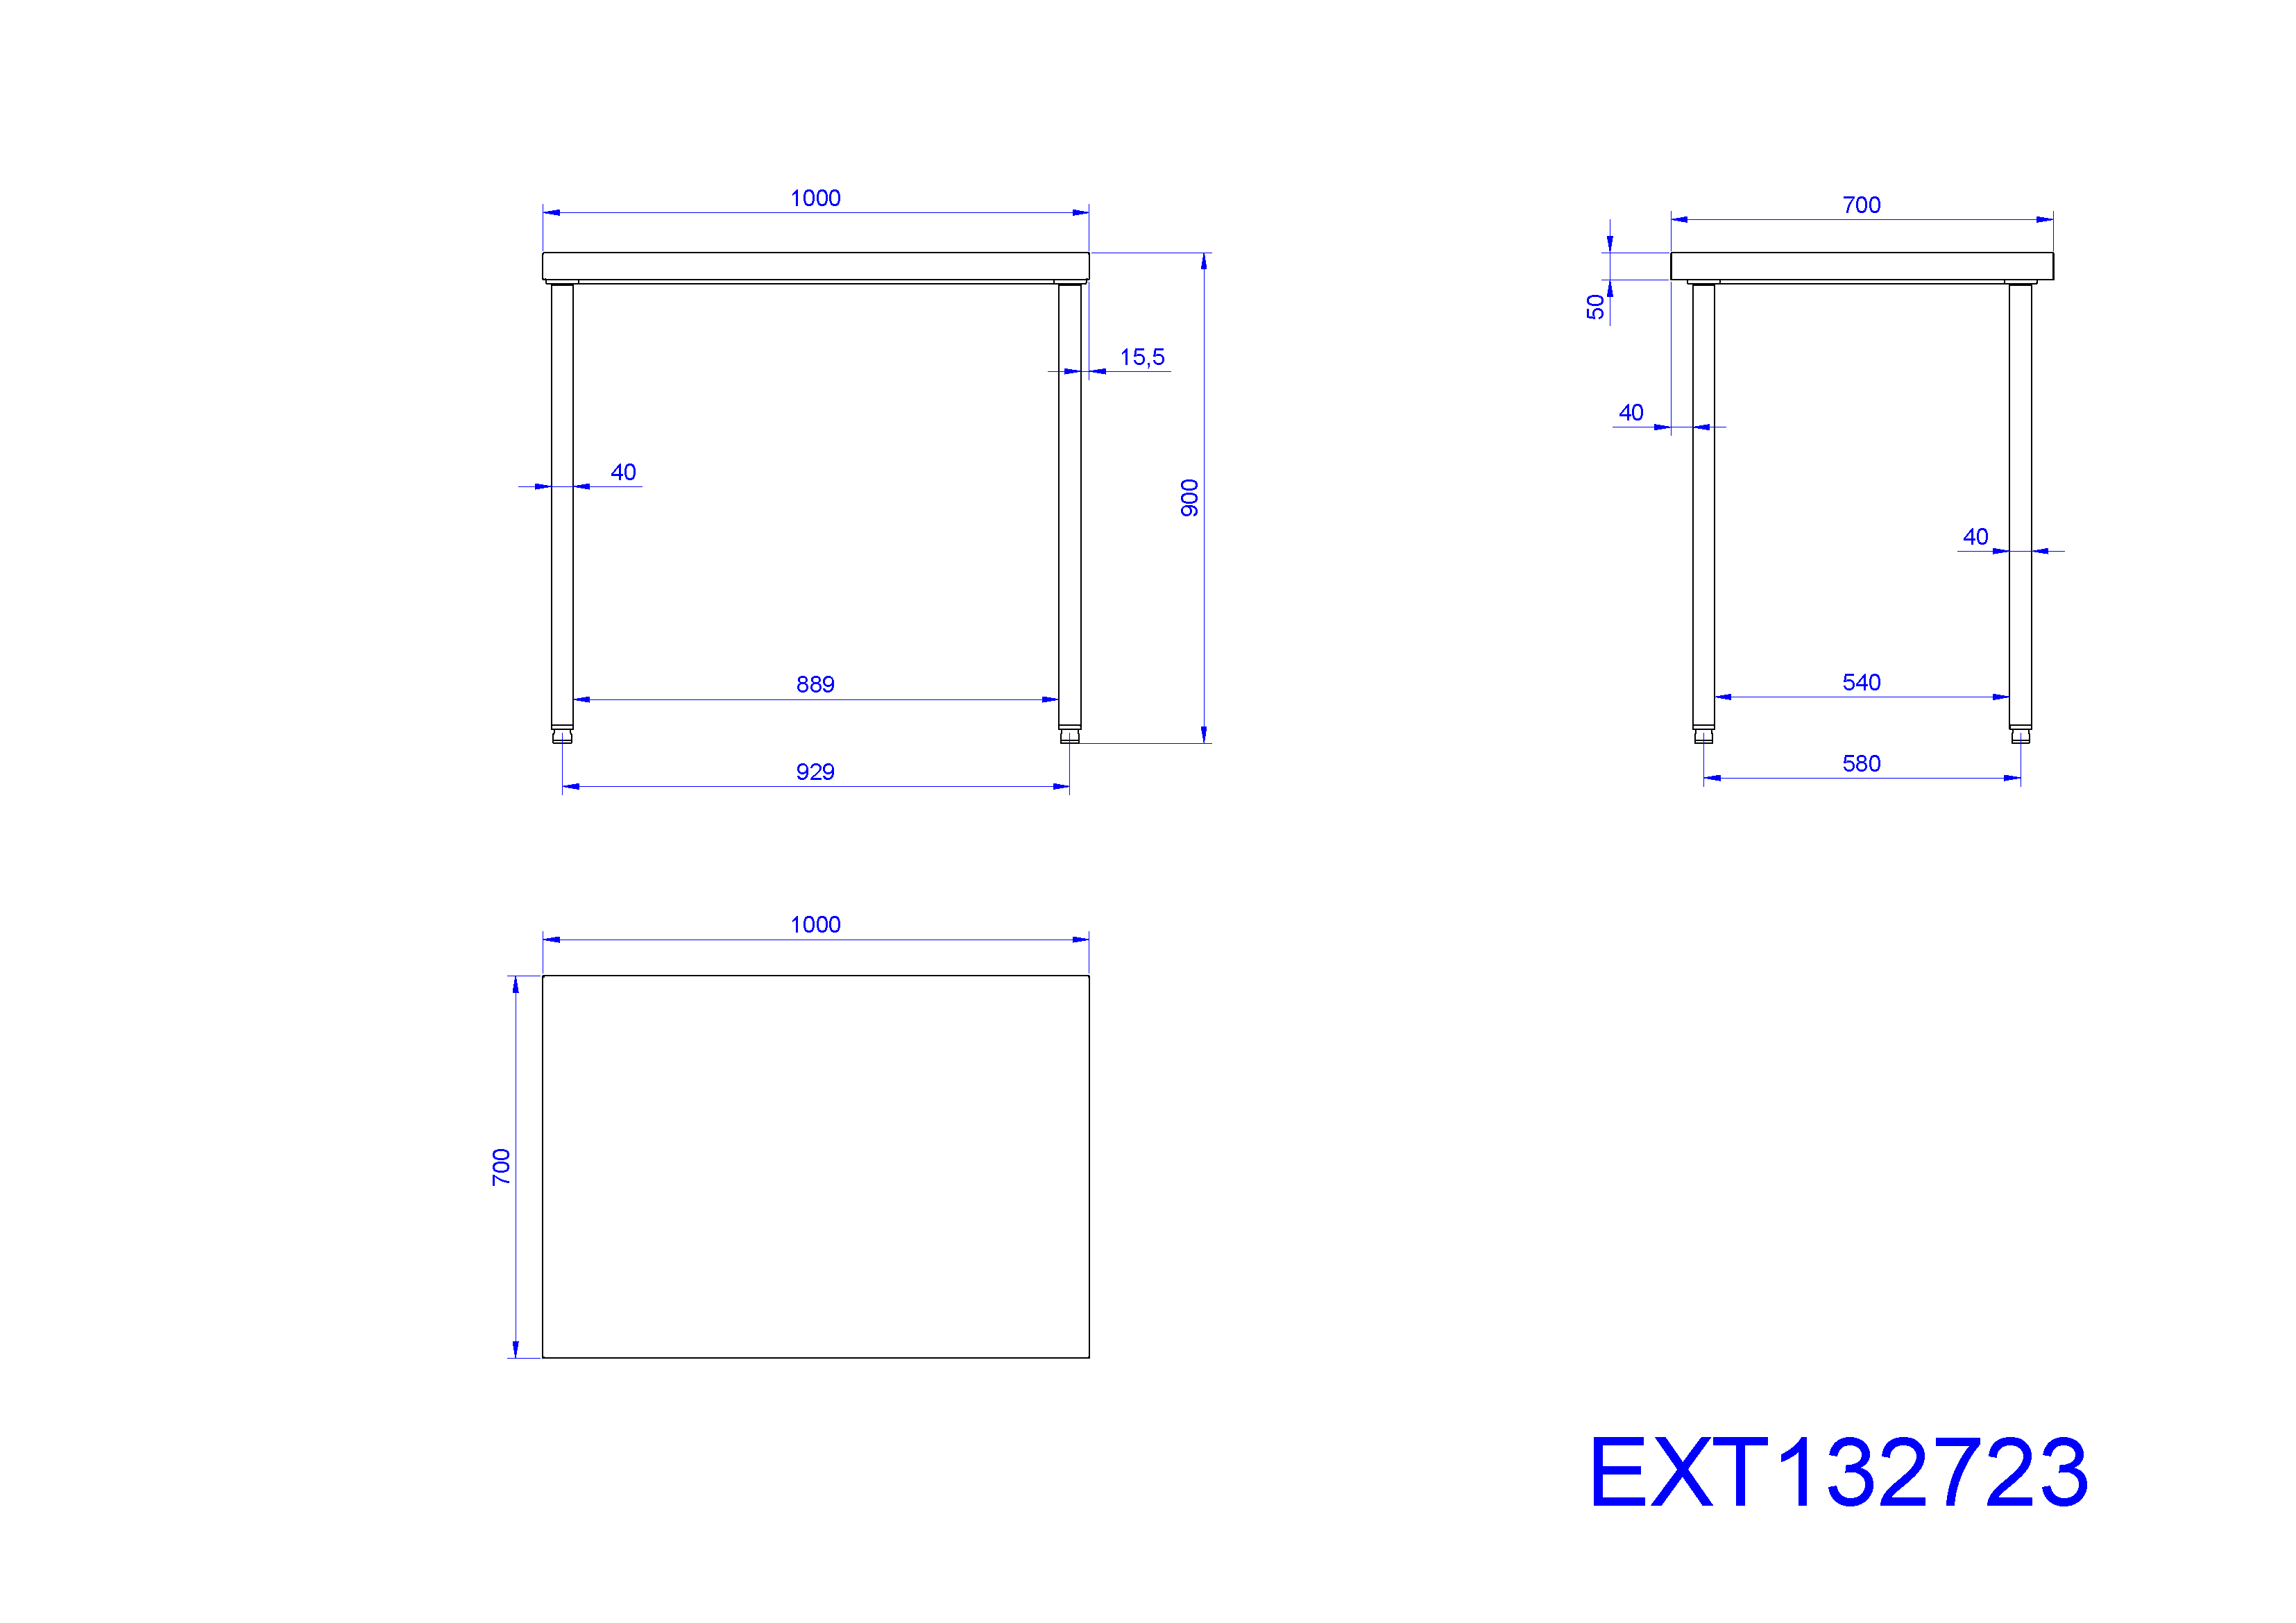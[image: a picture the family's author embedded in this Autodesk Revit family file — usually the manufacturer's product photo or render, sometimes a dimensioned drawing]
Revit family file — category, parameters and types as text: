
# Revit family: QF_ELECTROLUXPROFESSIONAL_132918_ML2S1217N
name_source: partatom
category: Attrezzature speciali
units: mm (PartAtom-declared; Revit-internal decimal feet)

## family parameters
Basato su piano di lavoro = No
Condiviso = No
Punto di calcolo locali = No
Quota connettore circolare = Usa diametro
Sempre verticale = Sì
Taglio con vuoti quando caricato = No
Tipo di parte = Normale

## types (1)
- Standard
    Accessory = Sì
    Cold Water Size = 0 mm
    Compressed Air Pressure = 0.0 Pa
    Compressed Air Size = 0 mm
    Compressed Air Volume = 0.0 L/s
    Condensate Return Size = 0 mm
    Cycle = 0 Hz
    Depth Actual = 700 mm  [stored 2.29659 ft]
    Descrizione = CUPBOARD SINK 2 BOWLS (500X500) 1200MM
    Direct Waste Size = 140 mm
    Gas Input Pressure = 0
    Gas KW = 0
    Gas Size = 0 mm
    HP = 0 HP
    Height Actual = 1000 mm  [stored 3.28084 ft]
    Hot Water Size = 0 mm
    Item Number = 132918
    Length Actual = 1200 mm
    Modello = ML2S1217N
    Phase = 0
    Produttore = Electrolux Professional
    Prospetto di default = 0 mm  [stored 0 ft]
    Refrigerant Compressor Remote = Sì
    Refrigeration Liquid Line Size = 0 mm  [stored 0 ft]
    Refrigeration Suction Line Size = 0 mm  [stored 0 ft]
    Steam Consumption per Hour = 0
    Steam Supply Maximum Pressure = 0.0 Pa
    Steam Supply Minimum Pressure = 0.0 Pa
    Steam Supply Size = 0 mm
    URL = https://www.electroluxprofessional.com
    URL Manufacturer = https://www.electroluxprofessional.com
    Volts = 0 V
    Watts = 0 W
    Weight = 55.00 kg

note: source unit labels omitted for Gas Input Pressure — the stored unit's dimension contradicts the parameter name (converter mislabeling)

note: [stored X ft] marks values corroborated as IEEE doubles in the binary element streams (Revit-internal decimal feet)

## geometry (parser evidence)
native form markers: Sweep x5
no freeform markers — native parametric forms only
